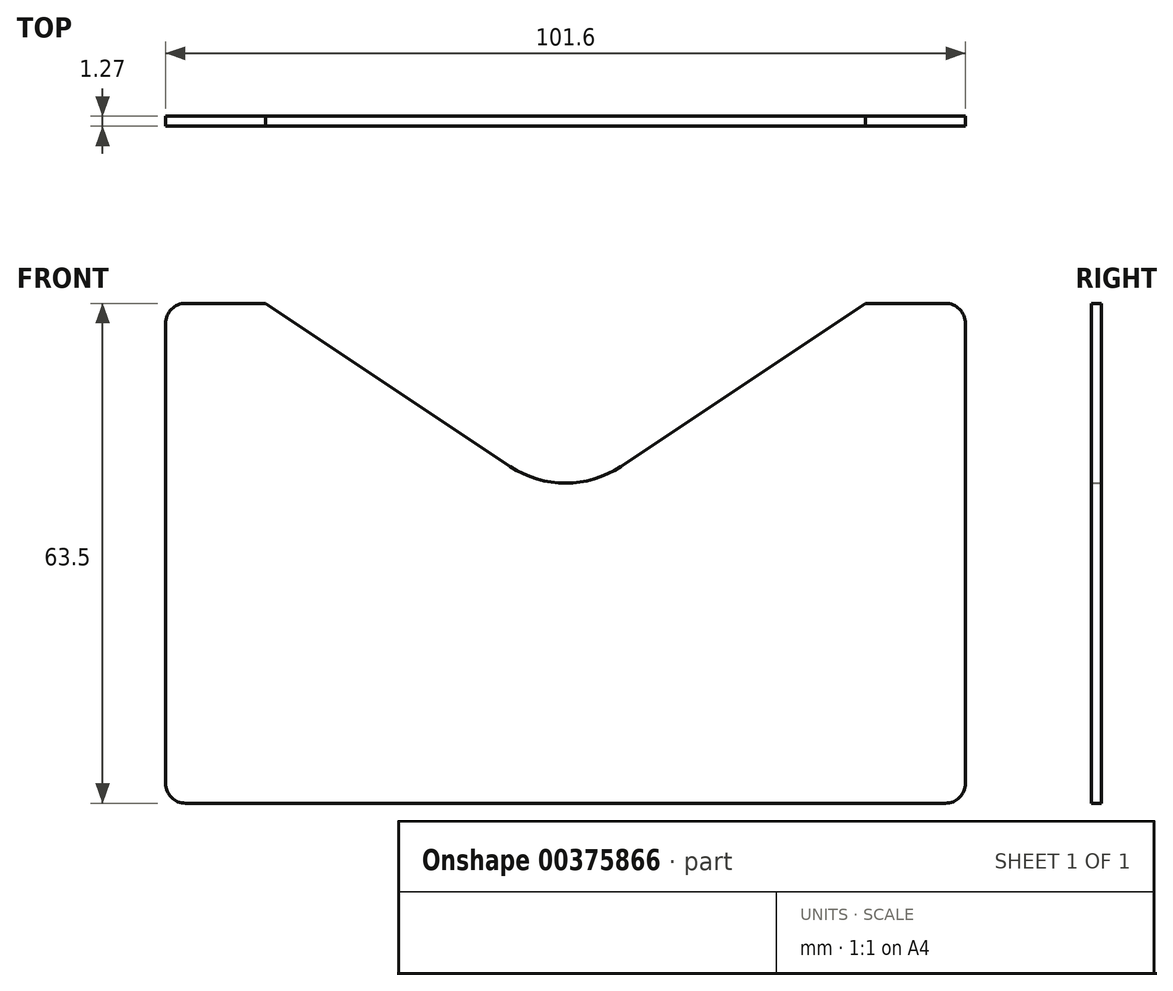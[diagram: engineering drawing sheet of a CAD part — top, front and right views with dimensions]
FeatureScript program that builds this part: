
annotation { "Feature Type Name" : "Feature", "Feature Type Description" : "" }
export const myFeature = defineFeature(function(context is Context, id is Id, definition is map)
    precondition{}
    {
        {
            var Q0;
            Q0=qCreatedBy(makeId("Front.planeOp"),FACE);
            var sketch = newSketch(context, id + "F0", { "sketchPlane" : qUnion([Q0])});
            skLineSegment(sketch, "E0.bottom", {"start": v(2.54, 0) * mm, "end": v(99.06, 0) * mm});
            skLineSegment(sketch, "E0.left", {"start": v(0, 2.54) * mm, "end": v(0, 60.96) * mm});
            skLineSegment(sketch, "E0.right", {"start": v(101.6, 2.54) * mm, "end": v(101.6, 60.96) * mm});
            skPoint(sketch, "E1.endSnap0", {"position": v(50.8, 57.15) * mm});
            skPoint(sketch, "E2.visualSharp", {"position": v(0, 0) * mm});
            skArc(sketch, "E2.filletArc", {"start": v(0, 2.54) * mm, "mid": v(0.74, 0.74) * mm, "end": v(2.54, 0) * mm});
            skPoint(sketch, "E3.visualSharp", {"position": v(101.6, 0) * mm});
            skArc(sketch, "E3.filletArc", {"start": v(99.06, 0) * mm, "mid": v(100.86, 0.74) * mm, "end": v(101.6, 2.54) * mm});
            skLineSegment(sketch, "E4", {"start": v(2.54, 63.5) * mm, "end": v(12.7, 63.5) * mm});
            skLineSegment(sketch, "E5", {"start": v(99.06, 63.5) * mm, "end": v(88.9, 63.5) * mm});
            skLineSegment(sketch, "E6", {"start": v(12.7, 63.5) * mm, "end": v(43.76, 42.8) * mm});
            skLineSegment(sketch, "E7", {"start": v(57.84, 42.8) * mm, "end": v(88.9, 63.5) * mm});
            skPoint(sketch, "E8.visualSharp", {"position": v(50.8, 38.1) * mm});
            skArc(sketch, "E8.filletArc", {"start": v(43.76, 42.8) * mm, "mid": v(50.8, 40.66) * mm, "end": v(57.84, 42.8) * mm});
            skPoint(sketch, "E9.visualSharp", {"position": v(0, 63.5) * mm});
            skArc(sketch, "E9.filletArc", {"start": v(2.54, 63.5) * mm, "mid": v(0.74, 62.76) * mm, "end": v(0, 60.96) * mm});
            skPoint(sketch, "E10.visualSharp", {"position": v(101.6, 63.5) * mm});
            skArc(sketch, "E10.filletArc", {"start": v(101.6, 60.96) * mm, "mid": v(100.86, 62.76) * mm, "end": v(99.06, 63.5) * mm});
            skSolve(sketch);
        }
        {
            var Q0;
            Q0=makeQuery(id+"F0.imprint","IMPRINT",FACE,{"disambiguationData":[TD([[makeQuery(id+"F0.imprint","IMPRINT",EDGE,{"derivedFrom":sQuery(id+"F0.wireOp",EDGE,"E0.bottom")}),1.0]])]});
            extrude(context, id + "F1", {"entities" : qUnion([Q0]), "depth" : 1.27 * mm});
        }
    });
